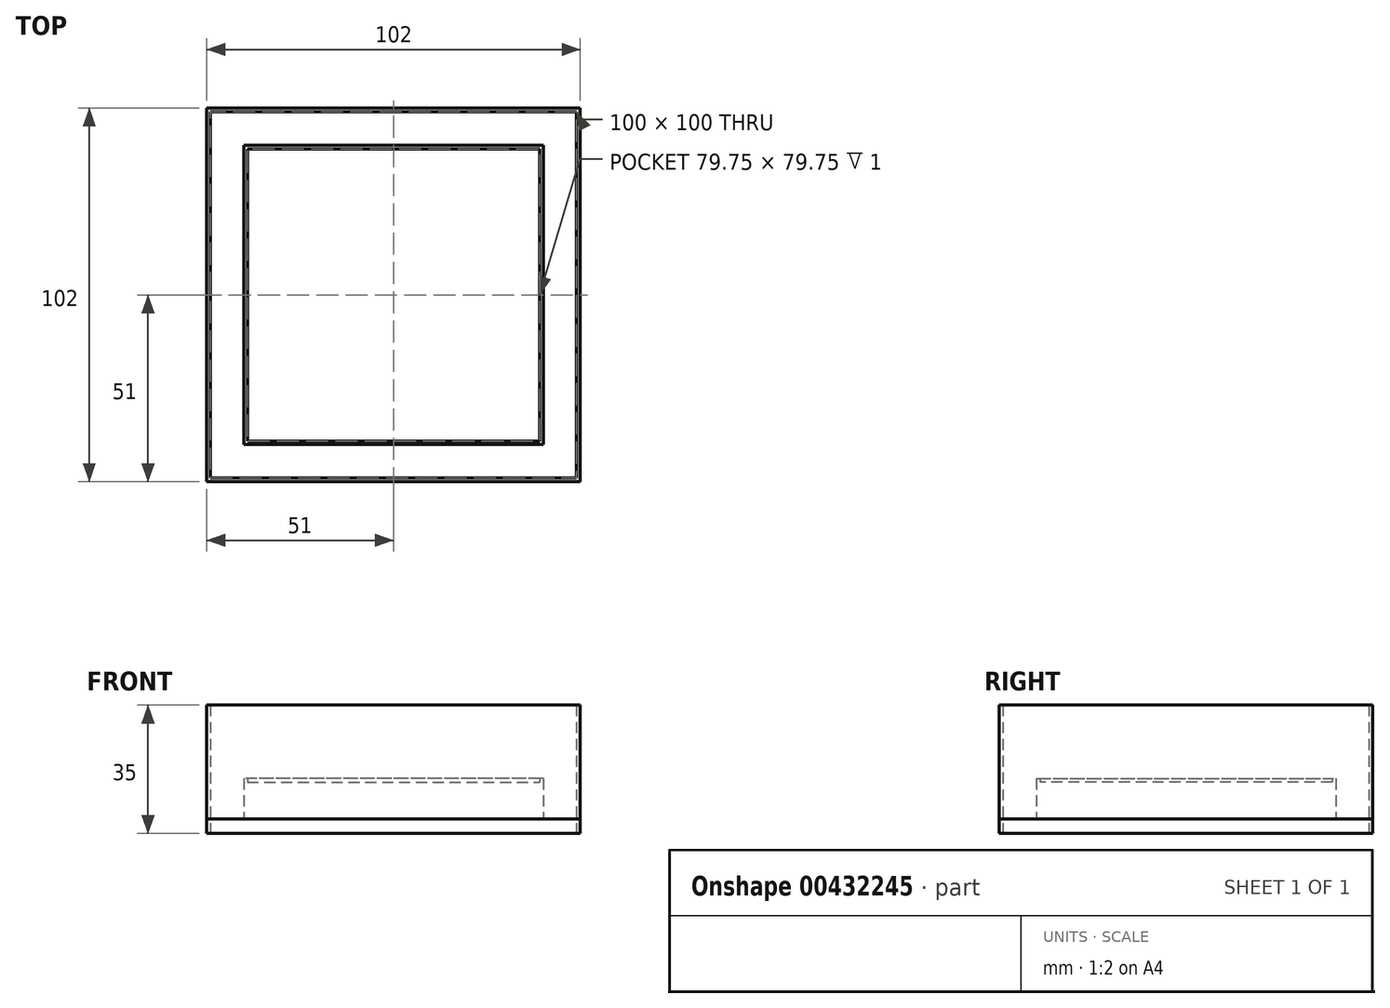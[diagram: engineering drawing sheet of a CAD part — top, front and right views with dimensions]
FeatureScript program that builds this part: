
annotation { "Feature Type Name" : "Feature", "Feature Type Description" : "" }
export const myFeature = defineFeature(function(context is Context, id is Id, definition is map)
    precondition{}
    {
        {
            var Q0;
            Q0=qCreatedBy(makeId("Top.planeOp"),FACE);
            var sketch = newSketch(context, id + "F0", { "sketchPlane" : qUnion([Q0])});
            skPoint(sketch, "E0.middle", {"position": v(0, 0) * mm});
            skLineSegment(sketch, "E1.bottom", {"start": v(51, -51) * mm, "end": v(-51, -51) * mm});
            skLineSegment(sketch, "E1.top", {"start": v(51, 51) * mm, "end": v(-51, 51) * mm});
            skLineSegment(sketch, "E1.left", {"start": v(51, -51) * mm, "end": v(51, 51) * mm});
            skLineSegment(sketch, "E1.right", {"start": v(-51, -51) * mm, "end": v(-51, 51) * mm});
            skSolve(sketch);
        }
        {
            var Q0;
            Q0=makeQuery(id+"F0.imprint","IMPRINT",FACE,{"disambiguationData":[TD([[makeQuery(id+"F0.imprint","IMPRINT",EDGE,{"derivedFrom":sQuery(id+"F0.wireOp",EDGE,"E1.bottom")}),-1.0]])]});
            extrude(context, id + "F1", {"entities" : qUnion([Q0]), "depth" : 4 * mm});
        }
        {
            var Q0;
            Q0=qCreatedBy(makeId("Top.planeOp"),FACE);
            var sketch = newSketch(context, id + "F2", { "sketchPlane" : qUnion([Q0])});
            skLineSegment(sketch, "E2.bottom", {"start": v(50, -50) * mm, "end": v(-50, -50) * mm});
            skLineSegment(sketch, "E2.top", {"start": v(50, 50) * mm, "end": v(-50, 50) * mm});
            skLineSegment(sketch, "E2.left", {"start": v(50, -50) * mm, "end": v(50, 50) * mm});
            skLineSegment(sketch, "E2.right", {"start": v(-50, -50) * mm, "end": v(-50, 50) * mm});
            skPoint(sketch, "E2.middle", {"position": v(0, 0) * mm});
            skLineSegment(sketch, "E3.bottom", {"start": v(51, -51) * mm, "end": v(-51, -51) * mm});
            skLineSegment(sketch, "E3.top", {"start": v(51, 51) * mm, "end": v(-51, 51) * mm});
            skLineSegment(sketch, "E3.left", {"start": v(51, -51) * mm, "end": v(51, 51) * mm});
            skLineSegment(sketch, "E3.right", {"start": v(-51, -51) * mm, "end": v(-51, 51) * mm});
            skSolve(sketch);
        }
        {
            var Q0;
            Q0 = qSketchRegion(id + "F2", true);
            var Q1;
            Q1 = qSketchRegion(id + "F4", true);
            extrude(context, id + "F3", {"entities" : qUnion([Q0, Q1]), "depth" : 35 * mm});
        }
        {
            var Q0;
            Q0=qCreatedBy(makeId("Top.planeOp"),FACE);
            var sketch = newSketch(context, id + "F4", { "sketchPlane" : qUnion([Q0])});
            skLineSegment(sketch, "E4.bottom", {"start": v(39.88, -39.87) * mm, "end": v(-39.88, -39.88) * mm});
            skLineSegment(sketch, "E4.top", {"start": v(39.88, 39.88) * mm, "end": v(-39.88, 39.88) * mm});
            skLineSegment(sketch, "E4.left", {"start": v(39.88, -39.87) * mm, "end": v(39.88, 39.88) * mm});
            skLineSegment(sketch, "E4.right", {"start": v(-39.88, -39.88) * mm, "end": v(-39.88, 39.88) * mm});
            skPoint(sketch, "E4.middle", {"position": v(0, 0) * mm});
            skLineSegment(sketch, "E5.bottom", {"start": v(40.88, -40.88) * mm, "end": v(-40.88, -40.88) * mm});
            skLineSegment(sketch, "E5.top", {"start": v(40.88, 40.88) * mm, "end": v(-40.88, 40.88) * mm});
            skLineSegment(sketch, "E5.left", {"start": v(40.88, -40.88) * mm, "end": v(40.88, 40.88) * mm});
            skLineSegment(sketch, "E5.right", {"start": v(-40.88, -40.88) * mm, "end": v(-40.88, 40.88) * mm});
            skSolve(sketch);
        }
        {
            var Q0;
            Q0 = qSketchRegion(id + "F4", true);
            extrude(context, id + "F5", {"entities" : qUnion([Q0]), "depth" : 15 * mm});
        }
        {
            var Q0;
            Q0=makeQuery(id+"F1.opExtrude","SWEPT_BODY",BODY,{"disambiguationData":[OSD([sQuery(id+"F0.wireOp",EDGE,"E1.bottom"),sQuery(id+"F0.wireOp",EDGE,"E1.top"),sQuery(id+"F0.wireOp",EDGE,"E1.left"),sQuery(id+"F0.wireOp",EDGE,"E1.right")])]});
            var Q1;
            Q1=makeQuery(id+"F5.opExtrude","SWEPT_BODY",BODY,{"disambiguationData":[OSD([sQuery(id+"F4.wireOp",EDGE,"E4.bottom"),sQuery(id+"F4.wireOp",EDGE,"E4.top"),sQuery(id+"F4.wireOp",EDGE,"E4.left"),sQuery(id+"F4.wireOp",EDGE,"E4.right"),sQuery(id+"F4.wireOp",EDGE,"E5.bottom"),sQuery(id+"F4.wireOp",EDGE,"E5.top"),sQuery(id+"F4.wireOp",EDGE,"E5.left"),sQuery(id+"F4.wireOp",EDGE,"E5.right")])]});
            booleanBodies(context, id + "F6", {"operationType" : BooleanOperationType.UNION, "tools" : qUnion([Q0, Q1])});
        }
        {
            var Q0;
            Q0=makeQuery(id+"F6.opBoolean","SPLIT",FACE,{"disambiguationData":[TD([makeQuery(id+"F5.opExtrude","SWEPT_FACE",FACE,{"disambiguationData":[OSD([sQuery(id+"F4.wireOp",EDGE,"E4.bottom")])]})])],"derivedFrom":makeQuery(id+"F1.opExtrude","CAP_FACE",FACE,{"disambiguationData":[OSD([sQuery(id+"F0.wireOp",EDGE,"E1.bottom"),sQuery(id+"F0.wireOp",EDGE,"E1.top"),sQuery(id+"F0.wireOp",EDGE,"E1.left"),sQuery(id+"F0.wireOp",EDGE,"E1.right")])],"isStart":false})});
            extrude(context, id + "F7", {"entities" : qUnion([Q0]), "operationType" : NewBodyOperationType.ADD, "depth" : 10 * mm});
        }
    });
